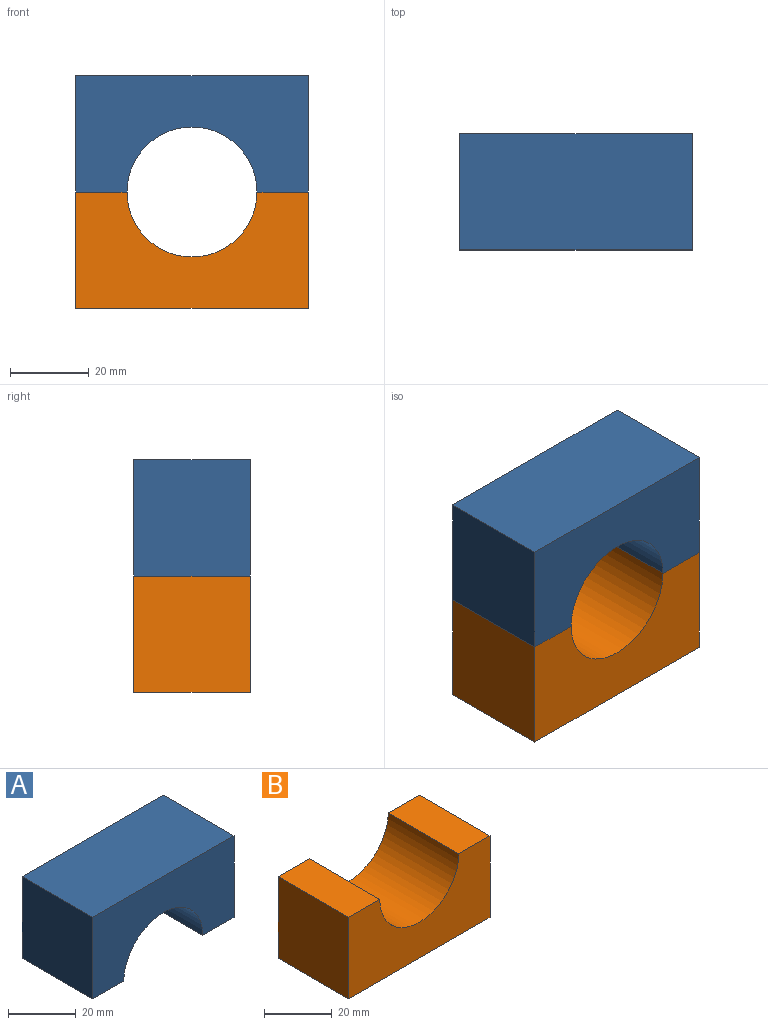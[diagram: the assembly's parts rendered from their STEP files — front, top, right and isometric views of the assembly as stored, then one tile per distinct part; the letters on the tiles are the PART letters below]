
ASSEMBLY  parts=2 mates=1
PART A: 8 faces, bbox 59x29.5x29.5 mm
  f0: plane 59x29.5mm, normal (0,-1,0), area 1312.9mm2, adj f2,f3,f4,f5,f6,f7
  f1: plane 59x29.5mm, normal (0,1,0), area 1312.9mm2, adj f2,f3,f4,f5,f6,f7
  f2: plane 29.5x29.5mm, normal (1,0,0), area 870.2mm2, adj f0,f1,f3,f6
  f3: plane 59x29.5mm, normal (0,0,1), area 1740.5mm2, adj f0,f1,f2,f4
  f4: plane 29.5x29.5mm, normal (-1,0,0), area 870.2mm2, adj f0,f1,f3,f7
  f5: cylinder r=16.5mm len=33mm, axis (0,-1,0), area 1529.2mm2, adj f0,f1,f6,f7
  f6: plane 29.5x13mm, normal (0,0,-1), area 383.5mm2, adj f0,f1,f2,f5
  f7: plane 29.5x13mm, normal (0,0,-1), area 383.5mm2, adj f0,f1,f4,f5
PART B: 8 faces, bbox 59x29.5x29.5 mm
  f0: plane 59x29.5mm, normal (0,-1,0), area 1312.9mm2, adj f1,f2,f3,f4,f6,f7
  f1: cylinder r=16.5mm len=33mm, axis (0,-1,0), area 1529.2mm2, adj f0,f5,f6,f7
  f2: plane 59x29.5mm, normal (0,0,-1), area 1740.5mm2, adj f0,f3,f4,f5
  f3: plane 29.5x29.5mm, normal (1,0,0), area 870.2mm2, adj f0,f2,f5,f6
  f4: plane 29.5x29.5mm, normal (-1,0,0), area 870.2mm2, adj f0,f2,f5,f7
  f5: plane 59x29.5mm, normal (0,1,0), area 1312.9mm2, adj f1,f2,f3,f4,f6,f7
  f6: plane 29.5x13mm, normal (0,0,1), area 383.5mm2, adj f0,f1,f3,f5
  f7: plane 29.5x13mm, normal (0,0,1), area 383.5mm2, adj f0,f1,f4,f5
PLACE A t=(-12.88,-34.66,-41.18)mm
PLACE B t=(-12.88,-34.66,-41.18)mm
MATE parallel A.f7 <-> B.f7  axis (0,0,-1) through (-35.88,-49.41,-41.18)mm
